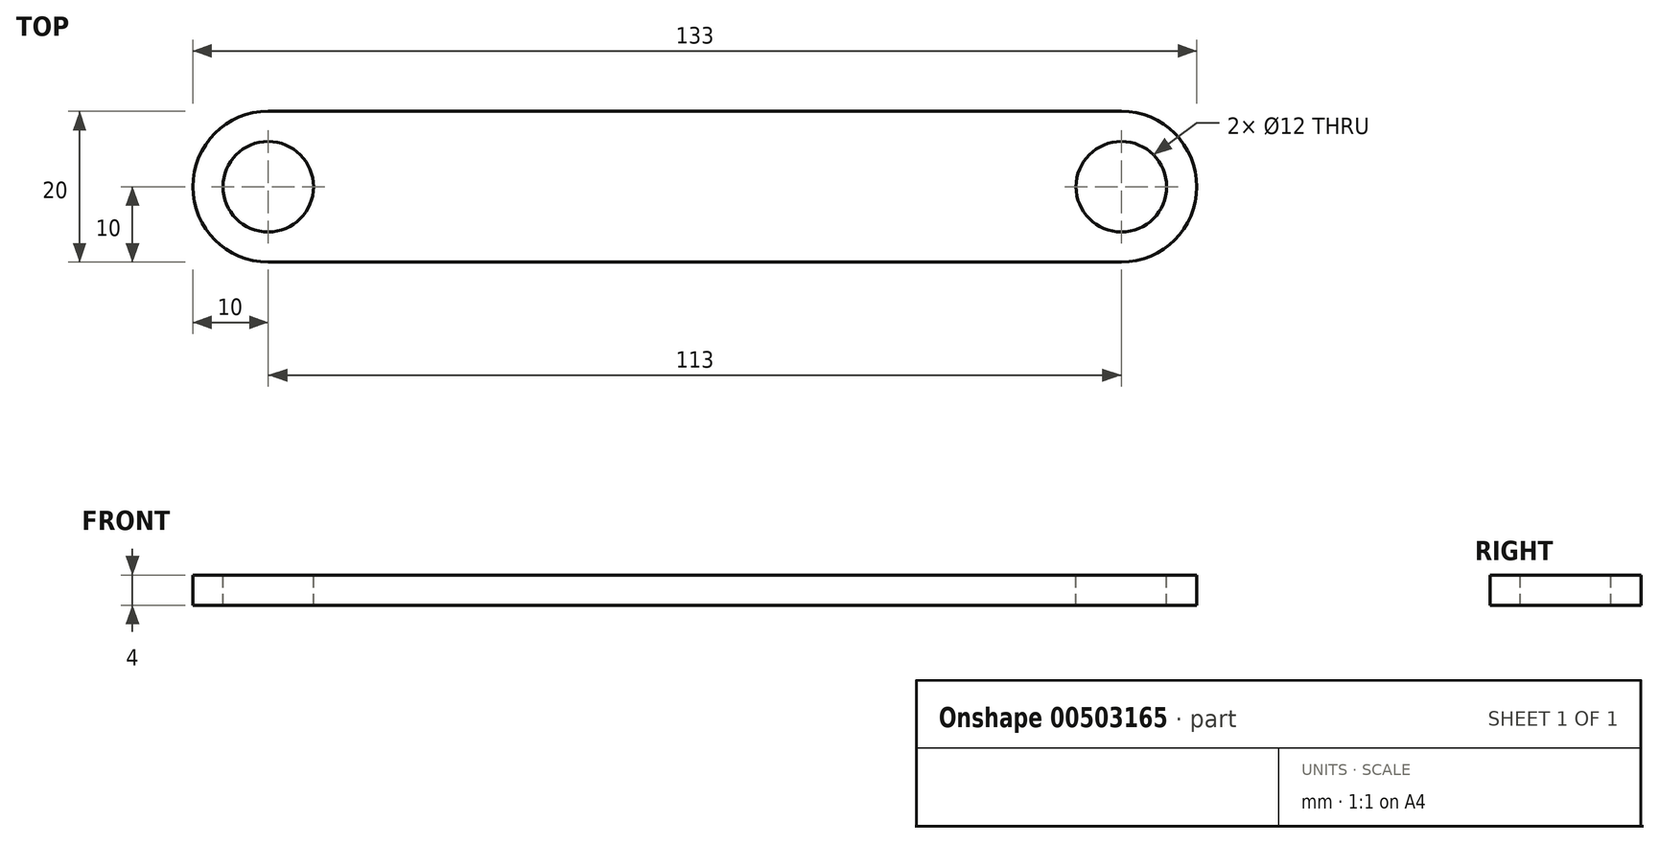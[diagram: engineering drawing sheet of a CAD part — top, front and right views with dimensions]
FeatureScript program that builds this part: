
annotation { "Feature Type Name" : "Feature", "Feature Type Description" : "" }
export const myFeature = defineFeature(function(context is Context, id is Id, definition is map)
    precondition{}
    {
        {
            var Q0;
            Q0=qCreatedBy(makeId("Top.planeOp"),FACE);
            var sketch = newSketch(context, id + "F0", { "sketchPlane" : qUnion([Q0])});
            skLineSegment(sketch, "E0.bottom", {"start": v(66.5, 10) * mm, "end": v(-66.5, 10) * mm});
            skLineSegment(sketch, "E0.top", {"start": v(66.5, -10) * mm, "end": v(-66.5, -10) * mm});
            skLineSegment(sketch, "E0.left", {"start": v(66.5, 10) * mm, "end": v(66.5, -10) * mm});
            skLineSegment(sketch, "E0.right", {"start": v(-66.5, 10) * mm, "end": v(-66.5, -10) * mm});
            skPoint(sketch, "E0.middle", {"position": v(0, 0) * mm});
            skSolve(sketch);
        }
        {
            var Q0;
            Q0=makeQuery(id+"F0.imprint","IMPRINT",FACE,{"disambiguationData":[TD([[makeQuery(id+"F0.imprint","IMPRINT",EDGE,{"derivedFrom":sQuery(id+"F0.wireOp",EDGE,"E0.bottom")}),1.0]])]});
            extrude(context, id + "F1", {"entities" : qUnion([Q0]), "depth" : 4 * mm});
        }
        {
            var Q0;
            Q0=makeQuery(id+"F1.opExtrude","CAP_FACE",FACE,{"disambiguationData":[OSD([sQuery(id+"F0.wireOp",EDGE,"E0.bottom"),sQuery(id+"F0.wireOp",EDGE,"E0.top"),sQuery(id+"F0.wireOp",EDGE,"E0.left"),sQuery(id+"F0.wireOp",EDGE,"E0.right")])],"isStart":false});
            var sketch = newSketch(context, id + "F2", { "sketchPlane" : qUnion([Q0])});
            skLineSegment(sketch, "E1", {"start": v(-66.5, 0) * mm, "end": v(-56.5, 0) * mm, "construction": true});
            skPoint(sketch, "E1.endSnap0", {"position": v(66.5, 0) * mm});
            skLineSegment(sketch, "E2", {"start": v(66.5, 0) * mm, "end": v(56.5, 0) * mm, "construction": true});
            skCircle(sketch, "E3", {"center": v(-56.5, 0) * mm, "radius": 6 * mm});
            skCircle(sketch, "E4", {"center": v(56.5, 0) * mm, "radius": 6 * mm});
            skSolve(sketch);
        }
        {
            var Q0;
            Q0=makeQuery(id+"F2.imprint","IMPRINT",FACE,{"disambiguationData":[TD([[makeQuery(id+"F2.imprint","IMPRINT",EDGE,{"derivedFrom":sQuery(id+"F2.wireOp",EDGE,"E3")}),1.0]])]});
            var Q1;
            Q1=makeQuery(id+"F2.imprint","IMPRINT",FACE,{"disambiguationData":[TD([[makeQuery(id+"F2.imprint","IMPRINT",EDGE,{"derivedFrom":sQuery(id+"F2.wireOp",EDGE,"E4")}),1.0]])]});
            extrude(context, id + "F3", {"entities" : qUnion([Q0, Q1]), "operationType" : NewBodyOperationType.REMOVE, "endBound" : BoundingType.THROUGH_ALL, "oppositeDirection" : true, "depth" : 25 * mm});
        }
        {
            var Q0;
            Q0=makeQuery(id+"F1.opExtrude","SWEPT_EDGE",EDGE,{"disambiguationData":[OSD([sQuery(id+"F0.wireOp",EDGE,"E0.top"),sQuery(id+"F0.wireOp",EDGE,"E0.right")])]});
            var Q1;
            Q1=makeQuery(id+"F1.opExtrude","SWEPT_EDGE",EDGE,{"disambiguationData":[OSD([sQuery(id+"F0.wireOp",EDGE,"E0.bottom"),sQuery(id+"F0.wireOp",EDGE,"E0.right")])]});
            var Q2;
            Q2=makeQuery(id+"F1.opExtrude","SWEPT_EDGE",EDGE,{"disambiguationData":[OSD([sQuery(id+"F0.wireOp",EDGE,"E0.top"),sQuery(id+"F0.wireOp",EDGE,"E0.left")])]});
            var Q3;
            Q3=makeQuery(id+"F1.opExtrude","SWEPT_EDGE",EDGE,{"disambiguationData":[OSD([sQuery(id+"F0.wireOp",EDGE,"E0.bottom"),sQuery(id+"F0.wireOp",EDGE,"E0.left")])]});
            fillet(context, id + "F4", {"entities" : qUnion([Q0, Q1, Q2, Q3]), "radius" : 10 * mm, "tangentPropagation" : true, "allowEdgeOverflow" : false});
        }
    });
